# Revit family: R-MBF-234
name_source: partatom
category: Portes
units: mm (PartAtom-declared; Revit-internal decimal feet)

## family parameters
Couper avec des vides une fois chargée = Non
Hôte = Mur
Partagée = Non
Point de calcul de pièce = Oui
Toujours verticalement = Oui

## types (1)
- MBF-234
    ----- EQUIPEMENTS ----------------------- = .
    ----- PARAMETRES DE L'HÔTE -------------------- = .
    ----- PARAMETRES DES VANTAUX -------------------- = .
    ----- PARAMETRES POSITION HUISSERIE -------------------- = .
    ----- PARAMETRES PROFIL HUISSERIE -------------------- = .
    ----- TYPE D'HUISSERIE -------------------- = .
    ----- TYPE DE VANTAIL -------------------- = .
    ----PARAMETRES INUTILISES------------------------- = .
    1 Vantail = Non
    2 Vantaux = Oui
    Coloris Oculus = Lauan - Meranti
    Coloris Oculus Métal = Acier - finition peinture thermolaque - gris - brillant
    Coloris Verre Oculus = Verre
    Coloris huisserie MDF = Pin
    Coloris_Chants = BER
    Construction analytique = <Aucun>
    DAS = Non
    Description = Bloc-porte bois RESISTANT AU FEU 2 vantaux SP51 sans point de fermeture avec battement feuilluré, simple action, EI60, sur huisserie bois
    Décalage Largeur Paumelle Recouvrement = 0 mm  [stored 0 ft]
    Décalage_Seuil_Vantail = 0 mm  [stored 0 ft]
    Désaffleurement_Vantail = 0 mm  [stored 0 ft]
    Epaisseurs_Vantaux = 51 mm
    Espacement_Paumelle_Vantail = 5 mm  [stored 0.0164042 ft]
    Fabricant = Malerba
    Ferrage_Encastre = Non
    Fiche Moati = Non
    Fiche_Produit = MBF-234
    Hauteur Feuillure Basse Vantail = 15 mm  [stored 0.0492126 ft]
    Hauteur joint APD = 1100 mm  [stored 3.60892 ft]
    Hauteur_Axe_Bequille = 1045 mm  [stored 3.42848 ft]
    Hauteur_Vantaux_Souhaitée = 2040 mm  [stored 6.69291 ft]
    Ht Microviseur = 1500 mm  [stored 4.92126 ft]
    Inv_Espacement_Paumelle_Vantail = 10 mm  [stored 0.0328084 ft]
    Inv_Position_Largeur_Paumelle = 5 mm  [stored 0.0164042 ft]
    Jeu Profondeur Recouvrement Vantail = 0 mm  [stored 0 ft]
    Jeu_Côté_Articulation_Vantail = 3 mm  [stored 0.00984252 ft]
    Jeu_Côté_Fermeture_Vantail = 2 mm  [stored 0.00656168 ft]
    Jeu_Traverse_Basse_Vantail = 5 mm  [stored 0.0164042 ft]
    Jeu_Traverse_Haute_Vantail = 3 mm  [stored 0.00984252 ft]
    Largeur Feuillure Battement Articulation = 15 mm  [stored 0.0492126 ft]
    Largeur_Axe_Bequille = 50 mm  [stored 0.164042 ft]
    Largeur_Feuillure_Battement_Semi_Fixe = 15 mm  [stored 0.0492126 ft]
    Largeur_Feuillure_Battement_Service = 15 mm  [stored 0.0492126 ft]
    Largeur_Feuillure_Profil = 15 mm  [stored 0.0492126 ft]
    Largeur_Vantail_Semi_Fixe_Souhaitée = 630 mm  [stored 2.06693 ft]
    Largeur_Vantail_Service_Souhaitée = 930 mm  [stored 3.05118 ft]
    Materiaux_Dominant = Bois
    Maternelle = Non
    Microviseur = Non
    Modèle = 44 - SA-HB
    Note d'identification = 2V SP51 - SPF - FEUILLURE - HUISSERIE BOIS
    Paumelle = Oui
    Paumelle_1 = 230 mm  [stored 0.754593 ft]
    Paumelle_2 = 809 mm  [stored 2.6542 ft]
    Paumelle_3 = 809 mm  [stored 2.6542 ft]
    Paumelle_4 = 165 mm
    Pivot_PMT = Non
    Position_Largeur_Paumelle = 0 mm  [stored 0 ft]
    Profondeur Feuillure Basse Vantail = 25 mm  [stored 0.082021 ft]
    Profondeur Feuillure Battement Articulation = 25 mm  [stored 0.082021 ft]
    Profondeur_Feuillure_Battement_Semi_Fixe = 37 mm  [stored 0.121391 ft]
    Profondeur_Feuillure_Battement_Service = 14 mm  [stored 0.0459318 ft]
    Profondeur_Feuillure_Profil = 59 mm
    Reference_Commerciale = 2V SP51 SPF
    Reprise_Doublage_1 = 30 mm  [stored 0.0984252 ft]
    Reprise_Doublage_2 = 30 mm  [stored 0.0984252 ft]
    Reprise_Doublage_Haut = 30 mm  [stored 0.0984252 ft]
    Resistance_Feu = EI60
    Sens_Feu = Recto / Verso
    Thermique (W/m2.°K) = 0
    URL = https://www.malerba.fr
    Vantail à Recouvrement = Non
    Visibilite_Paum-4 = Oui
    Visibilite_Poignee = Non
    X_Décalage Hauteur Feuillure Recouvrement = 0 mm  [stored 0 ft]
    X_Décalage Largeur Feuillure Recouvrement = 0 mm  [stored 0 ft]
    X_Décalage Largeur Recouvrement Vantail = 0 mm  [stored 0 ft]
    X_Décalage Profondeur Recouvrement Vantail = 0 mm  [stored 0 ft]
    X_Espacement_Paumelle_Vantail = 5 mm  [stored 0.0164042 ft]
    X_Fiche Moati = Non
    X_Inv Décalage Profondeur Recouvrement Vantail = 0 mm  [stored 0 ft]
    X_Inv_Espacement_Paumelle_Vantail = 0 mm  [stored 0 ft]
    X_Inv_Position_Largeur_Paumelle = 0 mm  [stored 0 ft]
    X_Paumelle = Oui

note: [stored X ft] marks values corroborated as IEEE doubles in the binary element streams (Revit-internal decimal feet)

## geometry (parser evidence)
native form markers: Blend x14
no freeform markers — native parametric forms only
